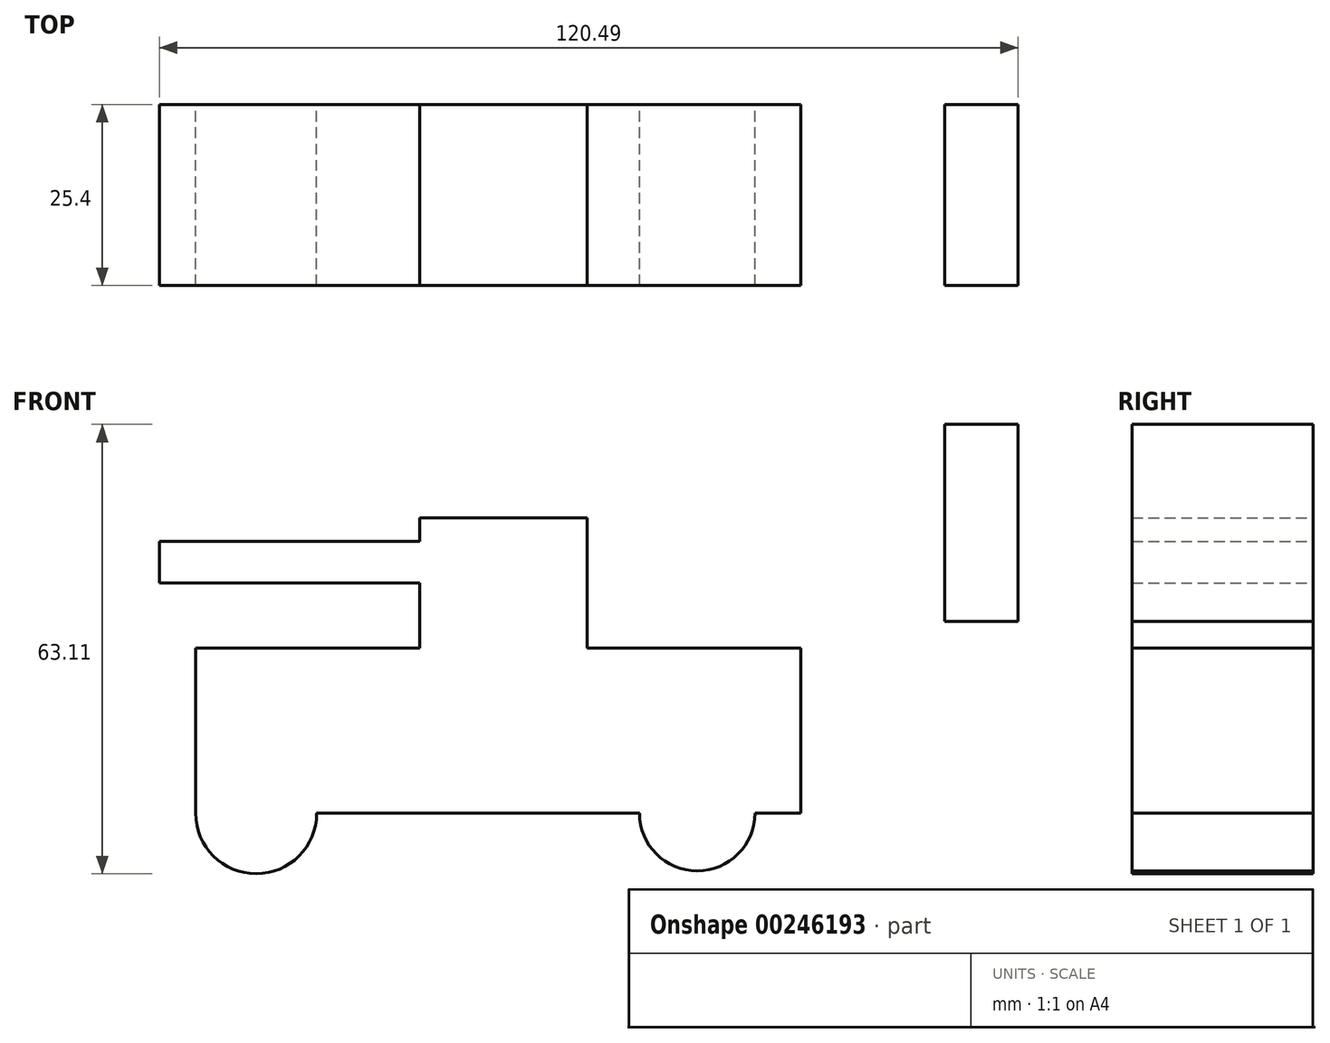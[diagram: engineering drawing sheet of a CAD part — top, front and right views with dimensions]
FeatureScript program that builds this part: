
annotation { "Feature Type Name" : "Feature", "Feature Type Description" : "" }
export const myFeature = defineFeature(function(context is Context, id is Id, definition is map)
    precondition{}
    {
        {
            var Q0;
            Q0=qCreatedBy(makeId("Front.planeOp"),FACE);
            var sketch = newSketch(context, id + "F0", { "sketchPlane" : qUnion([Q0])});
            skCircle(sketch, "E0", {"center": v(-31.96, 0) * mm, "radius": 8.5 * mm});
            skCircle(sketch, "E1", {"center": v(29.92, 0) * mm, "radius": 8.1 * mm});
            skLineSegment(sketch, "E2.bottom", {"start": v(-40.45, 0) * mm, "end": v(44.46, 0) * mm});
            skLineSegment(sketch, "E2.top", {"start": v(-40.45, 23.2) * mm, "end": v(44.46, 23.2) * mm});
            skLineSegment(sketch, "E2.left", {"start": v(-40.45, 0) * mm, "end": v(-40.45, 23.2) * mm});
            skLineSegment(sketch, "E2.right", {"start": v(44.46, 0) * mm, "end": v(44.46, 23.2) * mm});
            skArc(sketch, "E3", {"start": v(-16.49, 23.2) * mm, "mid": v(2.04, 5.78) * mm, "end": v(27.1, 10.08) * mm});
            skLineSegment(sketch, "E4.bottom", {"start": v(-8.99, 23.2) * mm, "end": v(14.45, 23.2) * mm});
            skLineSegment(sketch, "E4.top", {"start": v(-8.99, 41.49) * mm, "end": v(14.45, 41.49) * mm});
            skLineSegment(sketch, "E4.left", {"start": v(-8.99, 23.2) * mm, "end": v(-8.99, 41.49) * mm});
            skLineSegment(sketch, "E4.right", {"start": v(14.45, 23.2) * mm, "end": v(14.45, 41.49) * mm});
            skArc(sketch, "E5", {"start": v(64.61, 54.62) * mm, "mid": v(54.49, 38.94) * mm, "end": v(44.46, 23.2) * mm});
            skLineSegment(sketch, "E6.bottom", {"start": v(64.61, 54.62) * mm, "end": v(74.93, 54.62) * mm});
            skLineSegment(sketch, "E6.top", {"start": v(64.61, 26.96) * mm, "end": v(74.93, 26.96) * mm});
            skLineSegment(sketch, "E6.left", {"start": v(64.61, 54.62) * mm, "end": v(64.61, 26.96) * mm});
            skLineSegment(sketch, "E6.right", {"start": v(74.93, 54.62) * mm, "end": v(74.93, 26.96) * mm});
            skLineSegment(sketch, "E7.bottom", {"start": v(-8.99, 32.35) * mm, "end": v(-45.56, 32.35) * mm});
            skLineSegment(sketch, "E7.top", {"start": v(-8.99, 38.2) * mm, "end": v(-45.56, 38.2) * mm});
            skLineSegment(sketch, "E7.left", {"start": v(-8.99, 32.35) * mm, "end": v(-8.99, 38.2) * mm});
            skLineSegment(sketch, "E7.right", {"start": v(-45.56, 32.35) * mm, "end": v(-45.56, 38.2) * mm});
            skSolve(sketch);
        }
        {
            var Q0;
            Q0 = qSketchRegion(id + "F0", true);
            extrude(context, id + "F1", {"entities" : qUnion([Q0]), "depth" : 25.4 * mm});
        }
    });
